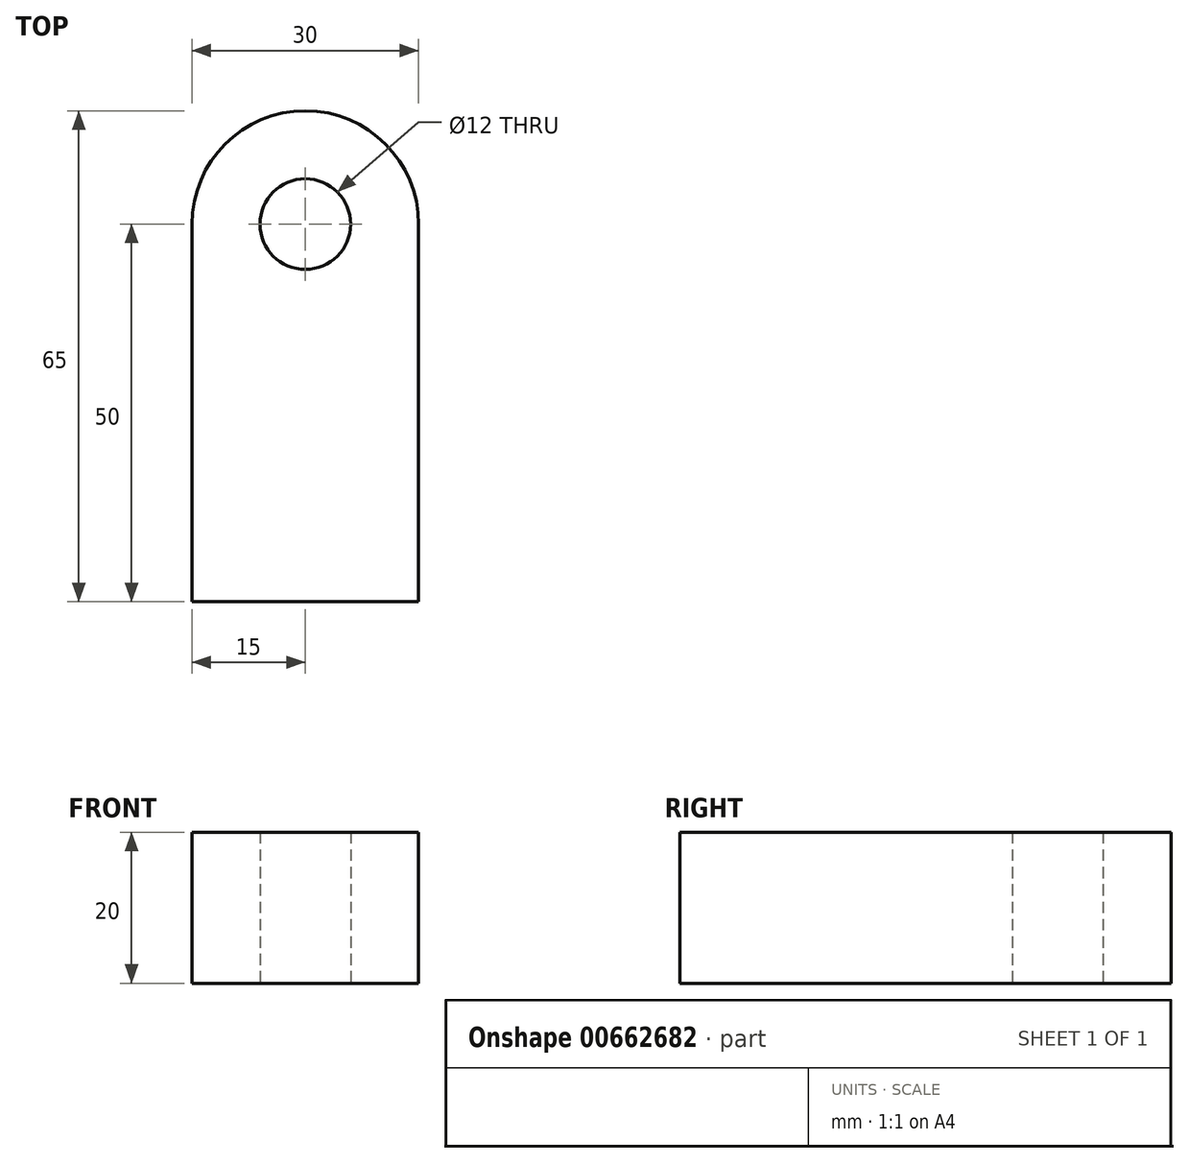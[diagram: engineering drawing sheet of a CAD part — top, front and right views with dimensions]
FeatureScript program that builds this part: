
annotation { "Feature Type Name" : "Feature", "Feature Type Description" : "" }
export const myFeature = defineFeature(function(context is Context, id is Id, definition is map)
    precondition{}
    {
        {
            var Q0;
            Q0=qCreatedBy(makeId("Top.planeOp"),FACE);
            var sketch = newSketch(context, id + "F0", { "sketchPlane" : qUnion([Q0])});
            skLineSegment(sketch, "E0", {"start": v(-15, 0) * mm, "end": v(-15, 50) * mm});
            skLineSegment(sketch, "E1", {"start": v(-15, 0) * mm, "end": v(15, 0) * mm});
            skLineSegment(sketch, "E2", {"start": v(15, 0) * mm, "end": v(15, 50) * mm});
            skArc(sketch, "E3", {"start": v(15, 50) * mm, "mid": v(0, 65) * mm, "end": v(-15, 50) * mm});
            skCircle(sketch, "E4", {"center": v(0, 50) * mm, "radius": 6 * mm});
            skSolve(sketch);
        }
        {
            var Q0;
            Q0=makeQuery(id+"F0.imprint","IMPRINT",FACE,{"disambiguationData":[TD([[makeQuery(id+"F0.imprint","IMPRINT",EDGE,{"derivedFrom":sQuery(id+"F0.wireOp",EDGE,"E0")}),-1.0]])]});
            extrude(context, id + "F1", {"entities" : qUnion([Q0]), "depth" : 20 * mm, "offsetDistance" : 25 * mm});
        }
    });
